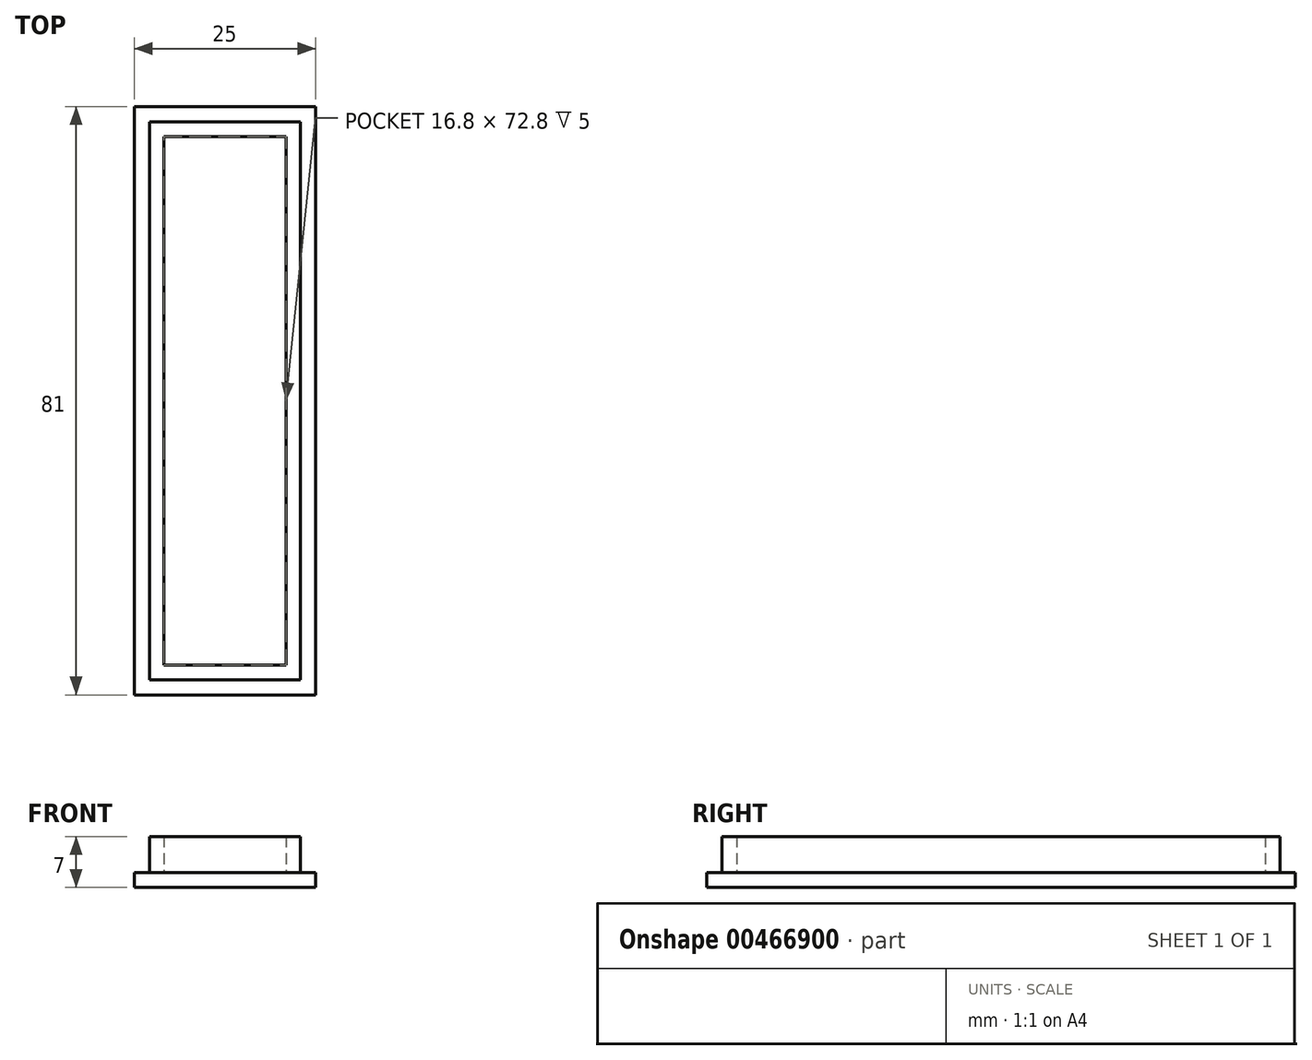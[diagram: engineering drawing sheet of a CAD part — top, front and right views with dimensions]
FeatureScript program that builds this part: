
annotation { "Feature Type Name" : "Feature", "Feature Type Description" : "" }
export const myFeature = defineFeature(function(context is Context, id is Id, definition is map)
    precondition{}
    {
        {
            var Q0;
            Q0=qCreatedBy(makeId("Top.planeOp"),FACE);
            var sketch = newSketch(context, id + "F0", { "sketchPlane" : qUnion([Q0])});
            skLineSegment(sketch, "E0", {"start": v(0, 0) * mm, "end": v(25, 0) * mm});
            skLineSegment(sketch, "E1", {"start": v(25, 0) * mm, "end": v(25, 81) * mm});
            skLineSegment(sketch, "E2", {"start": v(25, 81) * mm, "end": v(0, 81) * mm});
            skLineSegment(sketch, "E3", {"start": v(0, 81) * mm, "end": v(0, 0) * mm});
            skSolve(sketch);
        }
        {
            var Q0;
            Q0=makeQuery(id+"F0.imprint","IMPRINT",FACE,{"disambiguationData":[TD([[makeQuery(id+"F0.imprint","IMPRINT",EDGE,{"derivedFrom":sQuery(id+"F0.wireOp",EDGE,"E0")}),1.0]])]});
            extrude(context, id + "F1", {"entities" : qUnion([Q0]), "oppositeDirection" : true, "depth" : 2 * mm});
        }
        {
            var Q0;
            Q0=qCreatedBy(makeId("Top.planeOp"),FACE);
            var sketch = newSketch(context, id + "F2", { "sketchPlane" : qUnion([Q0])});
            skLineSegment(sketch, "E4.0", {"start": v(2.1, 78.9) * mm, "end": v(2.1, 2.1) * mm});
            skLineSegment(sketch, "E4.1", {"start": v(22.9, 78.9) * mm, "end": v(2.1, 78.9) * mm});
            skLineSegment(sketch, "E4.2", {"start": v(22.9, 2.1) * mm, "end": v(22.9, 78.9) * mm});
            skLineSegment(sketch, "E4.3", {"start": v(2.1, 2.1) * mm, "end": v(22.9, 2.1) * mm});
            skLineSegment(sketch, "E5.0", {"start": v(4.1, 76.9) * mm, "end": v(4.1, 4.1) * mm});
            skLineSegment(sketch, "E5.1", {"start": v(20.9, 76.9) * mm, "end": v(4.1, 76.9) * mm});
            skLineSegment(sketch, "E5.2", {"start": v(20.9, 4.1) * mm, "end": v(20.9, 76.9) * mm});
            skLineSegment(sketch, "E5.3", {"start": v(4.1, 4.1) * mm, "end": v(20.9, 4.1) * mm});
            skSolve(sketch);
        }
        {
            var Q0;
            Q0 = qSketchRegion(id + "F2", true);
            extrude(context, id + "F3", {"entities" : qUnion([Q0]), "operationType" : NewBodyOperationType.ADD, "depth" : 5 * mm});
        }
    });
